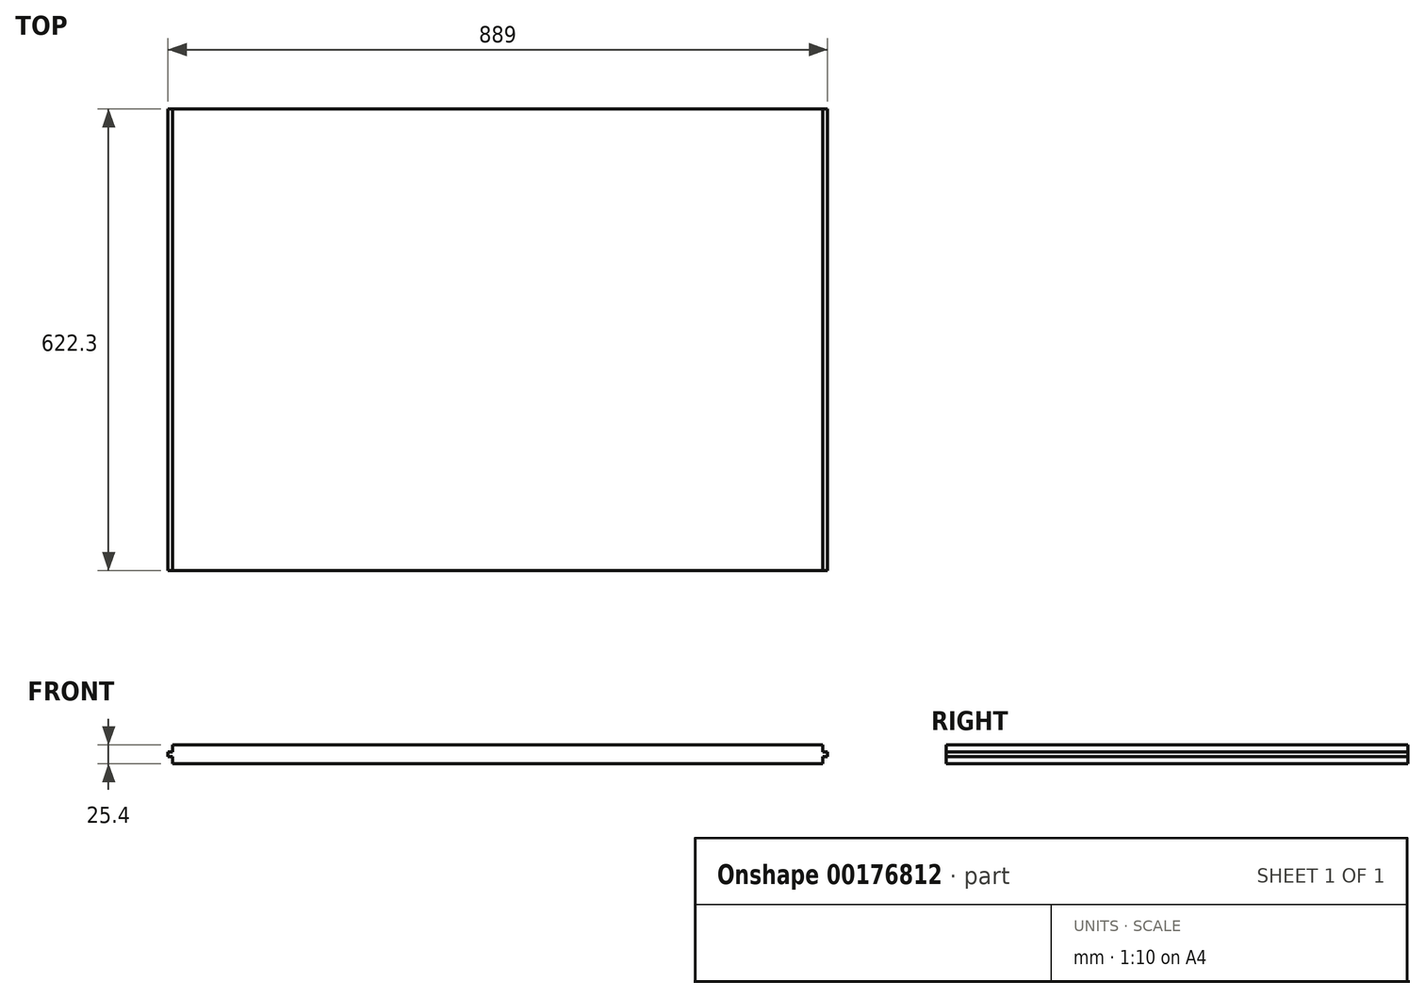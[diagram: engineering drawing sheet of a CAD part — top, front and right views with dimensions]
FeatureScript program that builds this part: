
annotation { "Feature Type Name" : "Feature", "Feature Type Description" : "" }
export const myFeature = defineFeature(function(context is Context, id is Id, definition is map)
    precondition{}
    {
        {
            var Q0;
            Q0=qCreatedBy(makeId("Top.planeOp"),FACE);
            var sketch = newSketch(context, id + "F0", { "sketchPlane" : qUnion([Q0])});
            skLineSegment(sketch, "E0.bottom", {"start": v(438.15, 311.15) * mm, "end": v(-438.15, 311.15) * mm});
            skLineSegment(sketch, "E0.top", {"start": v(438.15, -311.15) * mm, "end": v(-438.15, -311.15) * mm});
            skLineSegment(sketch, "E0.left", {"start": v(438.15, 311.15) * mm, "end": v(438.15, -311.15) * mm});
            skLineSegment(sketch, "E0.right", {"start": v(-438.15, 311.15) * mm, "end": v(-438.15, -311.15) * mm});
            skPoint(sketch, "E0.middle", {"position": v(0, 0) * mm});
            skSolve(sketch);
        }
        {
            var Q0;
            Q0 = qSketchRegion(id + "F0", true);
            extrude(context, id + "F1", {"entities" : qUnion([Q0]), "depth" : 25.4 * mm});
        }
        {
            var Q0;
            Q0=makeQuery(id+"F1.opExtrude","SWEPT_FACE",FACE,{"disambiguationData":[OSD([sQuery(id+"F0.wireOp",EDGE,"E0.top")])]});
            var sketch = newSketch(context, id + "F2", { "sketchPlane" : qUnion([Q0])});
            skLineSegment(sketch, "E1", {"start": v(0, 0) * mm, "end": v(0, 25.4) * mm});
            skLineSegment(sketch, "E2.bottom", {"start": v(-444.5, 15.87) * mm, "end": v(-431.8, 15.87) * mm});
            skLineSegment(sketch, "E2.top", {"start": v(-444.5, 9.52) * mm, "end": v(-431.8, 9.52) * mm});
            skLineSegment(sketch, "E2.left", {"start": v(-444.5, 15.87) * mm, "end": v(-444.5, 9.52) * mm});
            skLineSegment(sketch, "E2.right", {"start": v(-431.8, 15.87) * mm, "end": v(-431.8, 9.52) * mm});
            skPoint(sketch, "E2.middle", {"position": v(-438.15, 12.7) * mm});
            skLineSegment(sketch, "E3.MirrorCS", {"start": v(431.8, 15.88) * mm, "end": v(431.8, 9.53) * mm});
            skLineSegment(sketch, "E4.MirrorCS", {"start": v(444.5, 15.88) * mm, "end": v(444.5, 9.53) * mm});
            skLineSegment(sketch, "E5.MirrorCS", {"start": v(444.5, 9.53) * mm, "end": v(431.8, 9.53) * mm});
            skLineSegment(sketch, "E6.MirrorCS", {"start": v(444.5, 15.88) * mm, "end": v(431.8, 15.88) * mm});
            skPoint(sketch, "E7.MirrorP", {"position": v(438.15, 12.7) * mm});
            skSolve(sketch);
        }
        {
            var Q0;
            Q0 = qSketchRegion(id + "F2", true);
            extrude(context, id + "F3", {"entities" : qUnion([Q0]), "operationType" : NewBodyOperationType.ADD, "oppositeDirection" : true, "depth" : 622.3 * mm});
        }
    });
